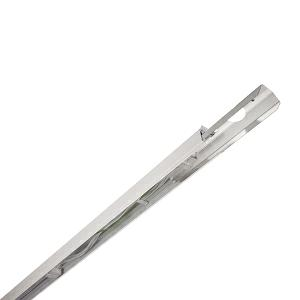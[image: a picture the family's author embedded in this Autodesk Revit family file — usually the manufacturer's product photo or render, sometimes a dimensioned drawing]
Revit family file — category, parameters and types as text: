
# Revit family: 3f_filippi_-_3f_linux_s_ip40_3f_filippi_-_a20024_-_3f_linux_s_7p_l3556
name_source: partatom
category: Lighting Fixtures
units: mm (PartAtom-declared; Revit-internal decimal feet)

## family parameters
Cut with Voids When Loaded = No
Host = Face
Light Source = No
Part Type = Normal
Room Calculation Point = No
Round Connector Dimension = Use Diameter
Shared = No

## types (1)
- 3F Filippi - 3F Linux S IP40
    Apparent Load = 0 VA
    Default Elevation = 1800 mm
    Description = Wired supporting structure for continuous channels, suitable for: lighting units 3F Linux L, 3F Linux D, 3F Linux DR, other luminaires or transport of electrical lines.

MECHANICAL
Wired base in hot galvanised steel and painted with polyester base in white colour, obtained through rolling process.
Saline-mist resistance equal to 500hrs and damp resistance equal to 700hrs.
Linear connecting element in hot galvanised steel already mounted on one end to form continuous channels.
Dimensions: 3556x62 mm, height 38 mm. Weight 4.1 kg.
IP40 protection degree.
Glow-wire test resistance 850°C.

ELECTRICAL
Through-wiring 7-poles with cables H07Z-U Halogen Free section 2.5 mm² HT90, with quick connecting terminal, irreversible, start / end and 2 intermediate power towers.

INSTALLATION
Ceiling / Suspended / Wall.
All accessories dedicated to this product are available on the Catalog and on our website www.3F-Filippi.com.

APPLICATIONS
Environments: commercial, exhibition areas, transit areas, lobbies or waiting rooms, shops, schools.

WARNING
Luminaire designed for disposal/recycling at end-of-life.
    Height = 38 mm
    Lamp = 0 x
    Length = 3556 mm
    Luminous efficacy = 0 lm/W
    Manufacturer = 3F Filippi
    ModVariant = No
    Model = 3F Filippi - A20024 - 3F Linux S 7P L3556
    Mounting Place = Ceiling
    Mounting Type = Pendant
    Number of Poles = 1
    OnlyDefault = Yes
    Power Factor = 1
    Product Name = 3F Filippi - 3F Linux S IP40
    Product group = Accessories
    ProductGroupID = 98
    Protection Class = Protection class
    Protection Degree = IP 40
    RLX_Detail_Level = 1
    RLX_Emergency_Light_Flux = 0 lm
    RLX_Emergency_Type = 0
    RLX_Emergency_Type_DB = No
    RlxData = <blob elided: 37337 chars, md5=8bc7c0b1>
    Standby Power = 0 W
    System Light Flux = 0 lm
    System Power = 0 W
    Type Comments = Product without accessories
    Type Image = 3ffilippi_3f_linux_s_ip40_l3556.jpg
    URL = http://relux.com
    VarID = ---
    Voltage = 0 V
    Weight = 0.00 kg
    Width = 62 mm  [stored 0.203412 ft]

note: [stored X ft] marks values corroborated as IEEE doubles in the binary element streams (Revit-internal decimal feet)

## geometry (parser evidence)
native form markers: Blend x4, Sweep x9
no freeform markers — native parametric forms only
